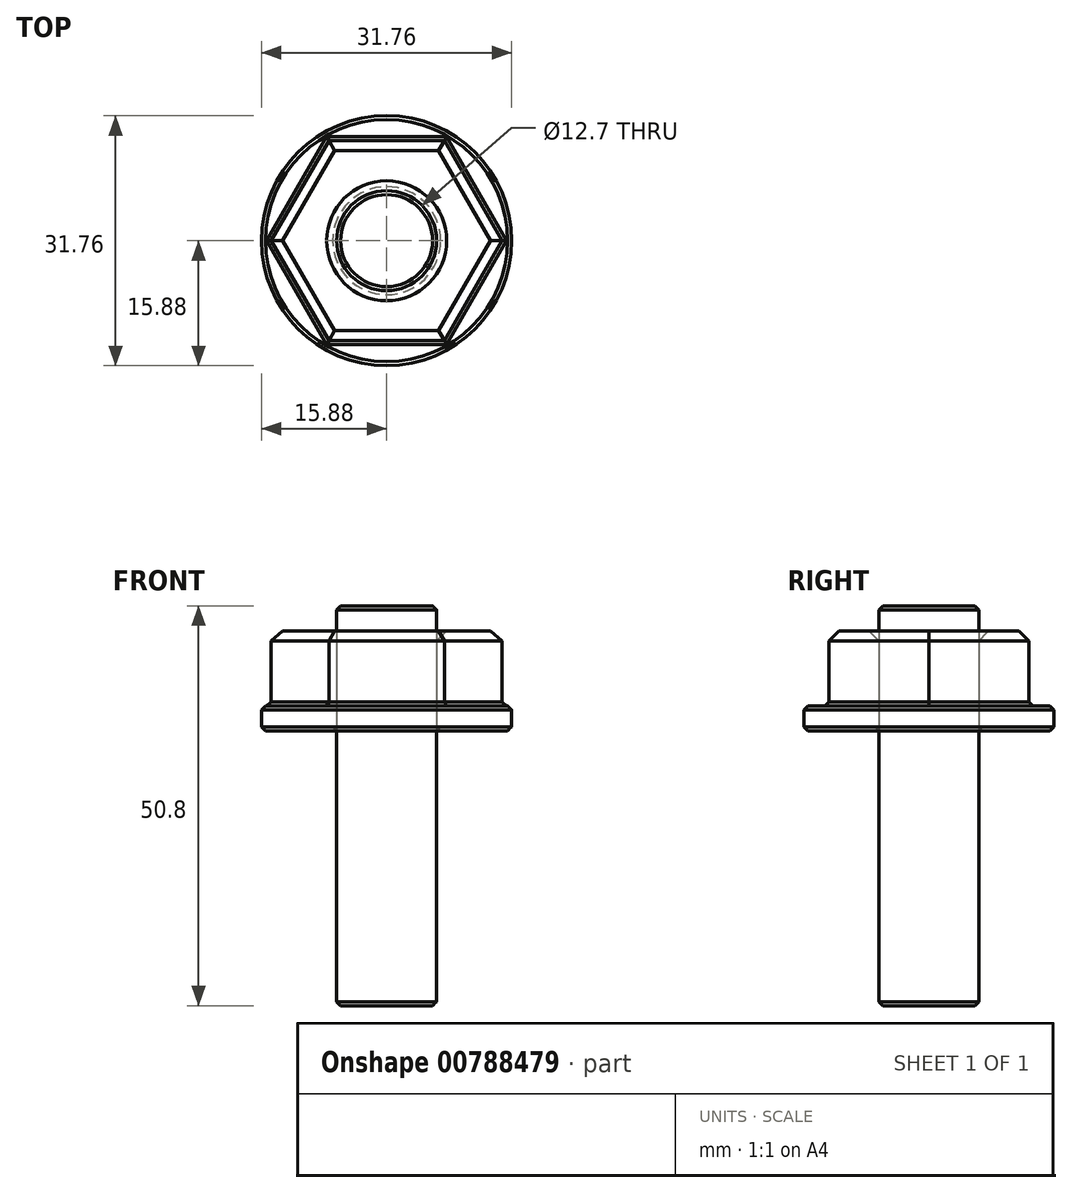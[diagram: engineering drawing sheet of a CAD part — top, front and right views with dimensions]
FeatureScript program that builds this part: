
annotation { "Feature Type Name" : "Feature", "Feature Type Description" : "" }
export const myFeature = defineFeature(function(context is Context, id is Id, definition is map)
    precondition{}
    {
        {
            var Q0;
            Q0=qCreatedBy(makeId("Top.planeOp"),FACE);
            var sketch = newSketch(context, id + "F0", { "sketchPlane" : qUnion([Q0])});
            skCircle(sketch, "E0", {"center": v(0, 0) * mm, "radius": 15.88 * mm});
            skCircle(sketch, "E1.cCircle", {"center": v(0, 0) * mm, "radius": 12.7 * mm, "construction": true});
            skLineSegment(sketch, "E1.0", {"start": v(-7.33, 12.7) * mm, "end": v(7.33, 12.7) * mm});
            skLineSegment(sketch, "E1.1", {"start": v(7.33, 12.7) * mm, "end": v(14.66, 0) * mm});
            skLineSegment(sketch, "E1.2", {"start": v(14.66, 0) * mm, "end": v(7.33, -12.7) * mm});
            skLineSegment(sketch, "E1.3", {"start": v(7.33, -12.7) * mm, "end": v(-7.33, -12.7) * mm});
            skLineSegment(sketch, "E1.4", {"start": v(-7.33, -12.7) * mm, "end": v(-14.66, 0) * mm});
            skLineSegment(sketch, "E1.5", {"start": v(-14.66, 0) * mm, "end": v(-7.33, 12.7) * mm});
            skPoint(sketch, "E1.0.midPoint", {"position": v(0, 12.7) * mm});
            skCircle(sketch, "E2", {"center": v(0, 0) * mm, "radius": 6.35 * mm});
            skSolve(sketch);
        }
        {
            var Q0;
            Q0=makeQuery(id+"F0.imprint","IMPRINT",FACE,{"disambiguationData":[TD([[makeQuery(id+"F0.imprint","IMPRINT",EDGE,{"derivedFrom":sQuery(id+"F0.wireOp",EDGE,"E0")}),1.0]])]});
            var Q1;
            Q1=makeQuery(id+"F0.imprint","IMPRINT",FACE,{"disambiguationData":[TD([[makeQuery(id+"F0.imprint","IMPRINT",EDGE,{"derivedFrom":sQuery(id+"F0.wireOp",EDGE,"E1.0")}),-1.0]])]});
            var Q2;
            Q2=makeQuery(id+"F0.imprint","IMPRINT",FACE,{"disambiguationData":[TD([[makeQuery(id+"F0.imprint","IMPRINT",EDGE,{"derivedFrom":sQuery(id+"F0.wireOp",EDGE,"E2")}),1.0]])]});
            extrude(context, id + "F1", {"entities" : qUnion([Q0, Q1, Q2]), "oppositeDirection" : true, "depth" : 3.17 * mm});
        }
        {
            var Q0;
            Q0=makeQuery(id+"F0.imprint","IMPRINT",FACE,{"disambiguationData":[TD([[makeQuery(id+"F0.imprint","IMPRINT",EDGE,{"derivedFrom":sQuery(id+"F0.wireOp",EDGE,"E1.0")}),-1.0]])]});
            extrude(context, id + "F2", {"entities" : qUnion([Q0]), "operationType" : NewBodyOperationType.ADD, "depth" : 9.52 * mm});
        }
        {
            var Q0;
            Q0=makeQuery(id+"F2.opExtrude","CAP_FACE",FACE,{"disambiguationData":[OSD([sQuery(id+"F0.wireOp",EDGE,"E1.0"),sQuery(id+"F0.wireOp",EDGE,"E1.1"),sQuery(id+"F0.wireOp",EDGE,"E1.2"),sQuery(id+"F0.wireOp",EDGE,"E1.3"),sQuery(id+"F0.wireOp",EDGE,"E1.4"),sQuery(id+"F0.wireOp",EDGE,"E1.5"),sQuery(id+"F0.wireOp",EDGE,"E2")])],"isStart":false});
            chamfer(context, id + "F3", {"entities" : qUnion([Q0]), "width" : 1.27 * mm, "tangentPropagation" : true});
        }
        {
            var Q0;
            Q0=makeQuery(id+"F0.imprint","IMPRINT",FACE,{"disambiguationData":[TD([[makeQuery(id+"F0.imprint","IMPRINT",EDGE,{"derivedFrom":sQuery(id+"F0.wireOp",EDGE,"E2")}),1.0]])]});
            extrude(context, id + "F4", {"entities" : qUnion([Q0]), "operationType" : NewBodyOperationType.REMOVE, "oppositeDirection" : true, "depth" : 25.4 * mm});
        }
        {
            var Q0;
            Q0=makeQuery(id+"F1.opExtrude","CAP_FACE",FACE,{"disambiguationData":[OSD([sQuery(id+"F0.wireOp",EDGE,"E0")])],"isStart":false});
            var Q1;
            {var subQ0=sQuery(id+"F0.wireOp",EDGE,"E0");Q1=makeQuery(id+"F2.boolean.opBoolean","SPLIT",FACE,{"disambiguationData":[TD([makeQuery(id+"F1.opExtrude","SWEPT_FACE",FACE,{"disambiguationData":[OSD([subQ0])]})])],"derivedFrom":makeQuery(id+"F1.opExtrude","CAP_FACE",FACE,{"disambiguationData":[OSD([subQ0])],"isStart":true})});}
            chamfer(context, id + "F5", {"entities" : qUnion([Q0, Q1]), "width" : 0.5 * mm, "tangentPropagation" : true});
        }
        {
            var Q0;
            Q0=makeQuery(id+"F0.imprint","IMPRINT",FACE,{"disambiguationData":[TD([[makeQuery(id+"F0.imprint","IMPRINT",EDGE,{"derivedFrom":sQuery(id+"F0.wireOp",EDGE,"E2")}),1.0]])]});
            extrude(context, id + "F6", {"entities" : qUnion([Q0]), "depth" : 12.7 * mm, "hasSecondDirection" : true, "secondDirectionOppositeDirection" : true, "secondDirectionDepth" : 38.1 * mm});
        }
        {
            var Q0;
            Q0=makeQuery(id+"F6.opExtrude","CAP_FACE",FACE,{"disambiguationData":[OSD([sQuery(id+"F0.wireOp",EDGE,"E2")])],"isStart":false});
            var Q1;
            Q1=makeQuery(id+"F6.opExtrude","CAP_FACE",FACE,{"disambiguationData":[OSD([sQuery(id+"F0.wireOp",EDGE,"E2")])],"isStart":true});
            chamfer(context, id + "F7", {"entities" : qUnion([Q0, Q1]), "width" : 0.5 * mm, "tangentPropagation" : true});
        }
    });
